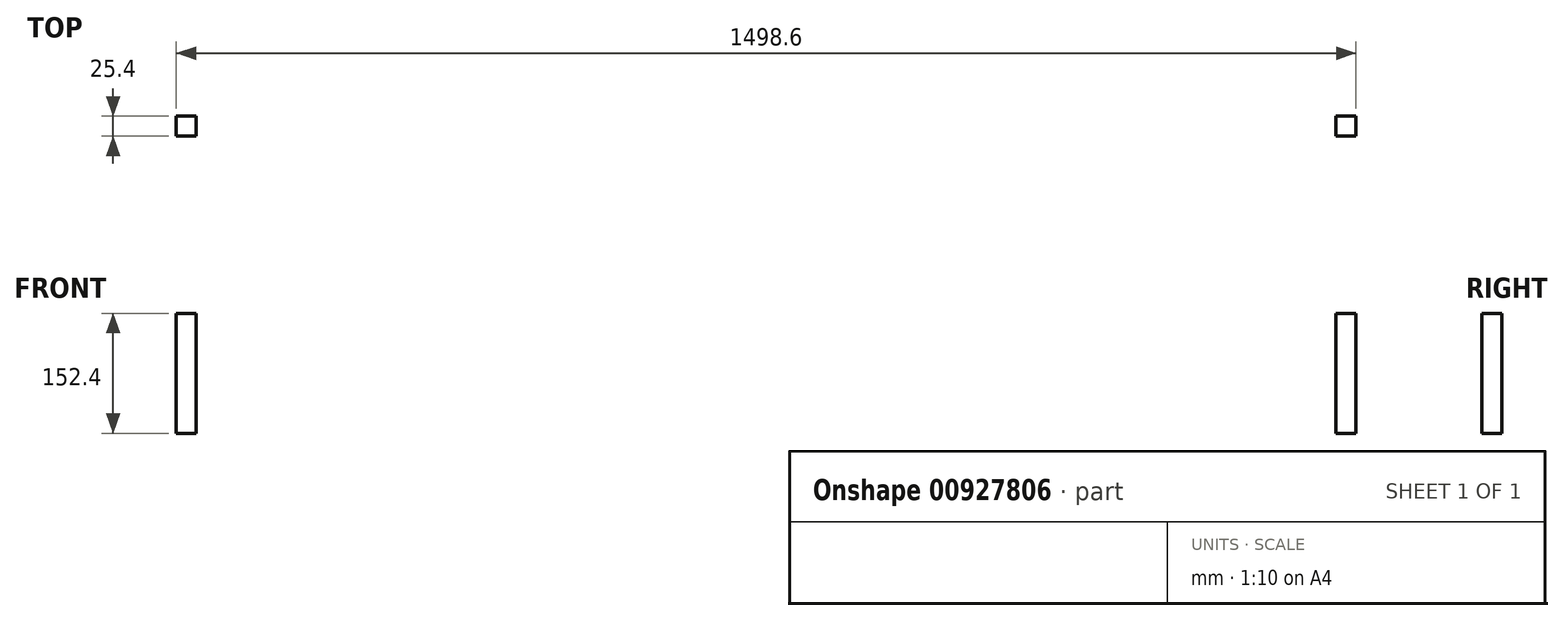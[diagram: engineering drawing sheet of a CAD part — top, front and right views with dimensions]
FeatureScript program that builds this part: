
annotation { "Feature Type Name" : "Feature", "Feature Type Description" : "" }
export const myFeature = defineFeature(function(context is Context, id is Id, definition is map)
    precondition{}
    {
        {
            var Q0;
            Q0=qCreatedBy(makeId("Top.planeOp"),FACE);
            var sketch = newSketch(context, id + "F0", { "sketchPlane" : qUnion([Q0])});
            skLineSegment(sketch, "E0.bottom", {"start": v(-749.3, 42.78) * mm, "end": v(-723.9, 42.78) * mm});
            skLineSegment(sketch, "E0.top", {"start": v(-749.3, 17.38) * mm, "end": v(-723.9, 17.38) * mm});
            skLineSegment(sketch, "E0.left", {"start": v(-749.3, 42.78) * mm, "end": v(-749.3, 17.38) * mm});
            skLineSegment(sketch, "E0.right", {"start": v(-723.9, 42.78) * mm, "end": v(-723.9, 17.38) * mm});
            skLineSegment(sketch, "E1.MirrorCS", {"start": v(723.9, 42.78) * mm, "end": v(723.9, 17.38) * mm});
            skLineSegment(sketch, "E2.MirrorCS", {"start": v(749.3, 42.78) * mm, "end": v(723.9, 42.78) * mm});
            skLineSegment(sketch, "E3.MirrorCS", {"start": v(749.3, 17.38) * mm, "end": v(723.9, 17.38) * mm});
            skLineSegment(sketch, "E4.MirrorCS", {"start": v(749.3, 42.78) * mm, "end": v(749.3, 17.38) * mm});
            skSolve(sketch);
        }
        {
            var Q0;
            Q0 = qSketchRegion(id + "F0", true);
            extrude(context, id + "F1", {"entities" : qUnion([Q0]), "depth" : 152.4 * mm, "offsetDistance" : 25.4 * mm});
        }
    });
